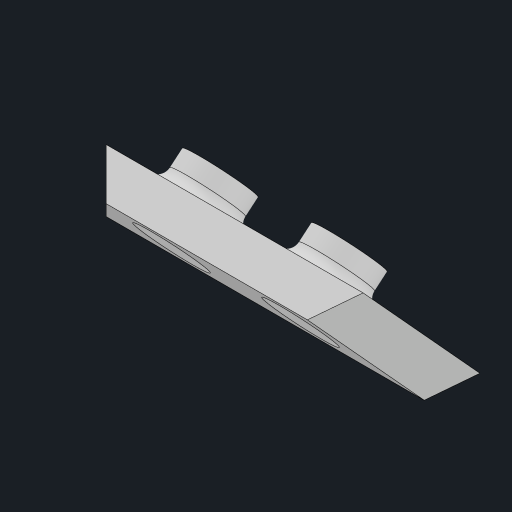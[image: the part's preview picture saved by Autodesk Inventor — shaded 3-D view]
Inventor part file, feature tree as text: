
AUTODESK INVENTOR PART (.ipt)
format: ipt  version: 2023 (Build 270158000, 158)  size: 198,656 bytes
history: native  units: mm
features: sketch x8, extrude x6, other x3, hole x1, fillet x1, chamfer x1, projected_geometry x1
ambient origin geometry x8: Origin, YZ Plane, XZ Plane, XY Plane, X Axis, Y Axis, Z Axis, Center Point
bodies: Body1 (feature_tree)
feature tree (21):
  other  "ソリッド1"
  extrude  "押し出し1"  Depth=40.0mm
  extrude  "押し出し2"  Depth=2.4mm
  other  "作業平面1"
  sketch  "スケッチ4"
  other  "作業平面2"
  extrude  "押し出し3"  Depth=50.0mm TaperAngle=0.0deg
  extrude  "押し出し4"  Depth=6.981317mm
  sketch  "スケッチ10"
  extrude  "押し出し6"  Depth=10.0mm
  hole  "穴1"  [1 undecoded]
  extrude  "押し出し5"  TaperAngle=90.0deg  [1 undecoded]
  fillet  "フィレット1"  Radius=14.2mm
  chamfer  "面取り1"  Distance=35.0mm
  sketch  "スケッチ1"
  sketch  "スケッチ2"
  sketch  "スケッチ5"
  sketch  "スケッチ6"
  sketch  "スケッチ7"
  projected_geometry  "投影ループ1"
  sketch  "スケッチ9"
note: 2 required parameter values undecoded (feature->parameter linkage not recoverable at this tier; creation-order binding heuristic only, values carry confidence <= 0.55)
